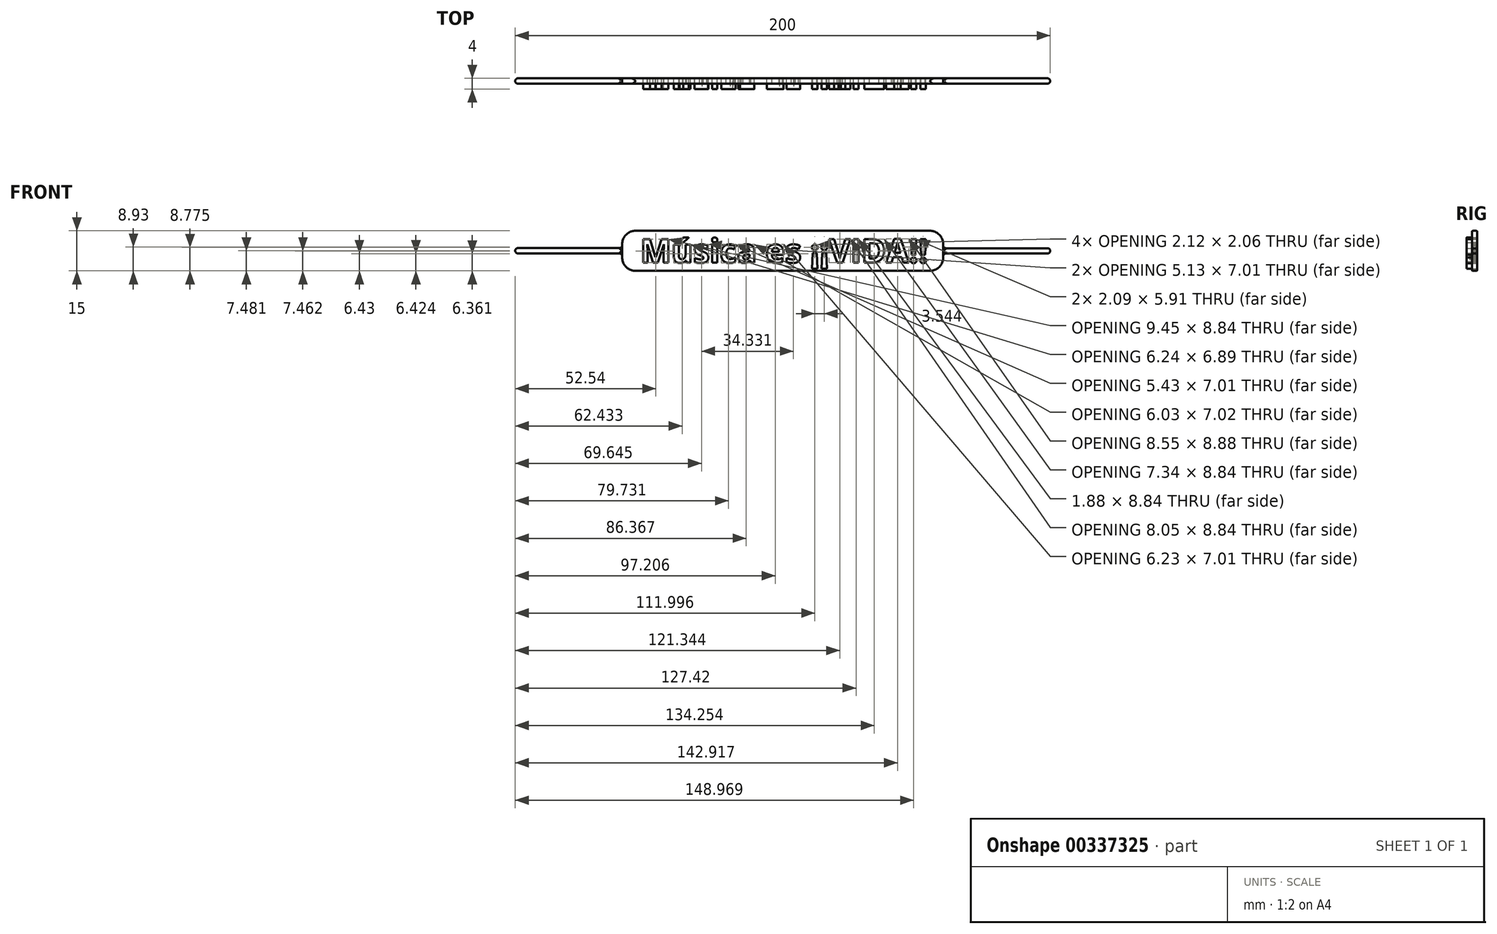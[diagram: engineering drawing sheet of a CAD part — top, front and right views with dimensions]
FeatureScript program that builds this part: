
annotation { "Feature Type Name" : "Feature", "Feature Type Description" : "" }
export const myFeature = defineFeature(function(context is Context, id is Id, definition is map)
    precondition{}
    {
        {
            var Q0;
            Q0=qCreatedBy(makeId("Front.planeOp"),FACE);
            var sketch = newSketch(context, id + "F0", { "sketchPlane" : qUnion([Q0])});
            skLineSegment(sketch, "E0.bottom", {"start": v(-55, 7.5) * mm, "end": v(55, 7.5) * mm});
            skLineSegment(sketch, "E0.top", {"start": v(-55, -7.5) * mm, "end": v(55, -7.5) * mm});
            skLineSegment(sketch, "E0.left", {"start": v(-60, 2.5) * mm, "end": v(-60, -2.5) * mm});
            skLineSegment(sketch, "E0.right", {"start": v(60, 2.5) * mm, "end": v(60, -2.5) * mm});
            skPoint(sketch, "E1.visualSharp", {"position": v(-60, 7.5) * mm});
            skArc(sketch, "E1.filletArc", {"start": v(-55, 7.5) * mm, "mid": v(-58.54, 6.04) * mm, "end": v(-60, 2.5) * mm});
            skPoint(sketch, "E2.visualSharp", {"position": v(-60, -7.5) * mm});
            skArc(sketch, "E2.filletArc", {"start": v(-60, -2.5) * mm, "mid": v(-58.54, -6.04) * mm, "end": v(-55, -7.5) * mm});
            skPoint(sketch, "E3.visualSharp", {"position": v(60, -7.5) * mm});
            skArc(sketch, "E3.filletArc", {"start": v(55, -7.5) * mm, "mid": v(58.54, -6.04) * mm, "end": v(60, -2.5) * mm});
            skPoint(sketch, "E4.visualSharp", {"position": v(60, 7.5) * mm});
            skArc(sketch, "E4.filletArc", {"start": v(60, 2.5) * mm, "mid": v(58.54, 6.04) * mm, "end": v(55, 7.5) * mm});
            skText(sketch, "E5", { "text": "Música es ¡¡VIDA!!", "fontName": "OpenSans-Bold.ttf"});
            const initialGuessF0  = {"E5": [-0.0533, -0.00446, 1, 0, 0.00892]};
            skSetInitialGuess(sketch, initialGuessF0);
            skSolve(sketch);
        }
        {
            var Q0;
            Q0 = qSketchRegion(id + "F0", true);
            var Q1;
            Q1=makeQuery(id+"F0.imprint","IMPRINT",FACE,{"disambiguationData":[TD([[makeQuery(id+"F0.imprint","IMPRINT",EDGE,{"derivedFrom":sQuery(id+"F0.wireOp",EDGE,"E5.sketch_text.stroke-110")}),1.0]])]});
            var Q2;
            Q2=makeQuery(id+"F0.imprint","IMPRINT",FACE,{"disambiguationData":[TD([[makeQuery(id+"F0.imprint","IMPRINT",EDGE,{"derivedFrom":sQuery(id+"F0.wireOp",EDGE,"E5.sketch_text.stroke-117")}),1.0]])]});
            var Q3;
            Q3=makeQuery(id+"F0.imprint","IMPRINT",FACE,{"disambiguationData":[TD([[makeQuery(id+"F0.imprint","IMPRINT",EDGE,{"derivedFrom":sQuery(id+"F0.wireOp",EDGE,"E5.sketch_text.stroke-208")}),1.0]])]});
            var Q4;
            Q4=makeQuery(id+"F0.imprint","IMPRINT",FACE,{"disambiguationData":[TD([[makeQuery(id+"F0.imprint","IMPRINT",EDGE,{"derivedFrom":sQuery(id+"F0.wireOp",EDGE,"E5.sketch_text.stroke-221")}),1.0]])]});
            extrude(context, id + "F1", {"entities" : qUnion([Q0, Q1, Q2, Q3, Q4]), "depth" : 2 * mm});
        }
        {
            var Q0;
            Q0=makeQuery(id+"F0.imprint","IMPRINT",FACE,{"disambiguationData":[TD([[makeQuery(id+"F0.imprint","IMPRINT",EDGE,{"derivedFrom":sQuery(id+"F0.wireOp",EDGE,"E5.sketch_text.stroke-0")}),-1.0]])]});
            var Q1;
            Q1=makeQuery(id+"F0.imprint","IMPRINT",FACE,{"disambiguationData":[TD([[makeQuery(id+"F0.imprint","IMPRINT",EDGE,{"derivedFrom":sQuery(id+"F0.wireOp",EDGE,"E5.sketch_text.stroke-19")}),-1.0]])]});
            var Q2;
            Q2=makeQuery(id+"F0.imprint","IMPRINT",FACE,{"disambiguationData":[TD([[makeQuery(id+"F0.imprint","IMPRINT",EDGE,{"derivedFrom":sQuery(id+"F0.wireOp",EDGE,"E5.sketch_text.stroke-36")}),-1.0]])]});
            var Q3;
            Q3=makeQuery(id+"F0.imprint","IMPRINT",FACE,{"disambiguationData":[TD([[makeQuery(id+"F0.imprint","IMPRINT",EDGE,{"derivedFrom":sQuery(id+"F0.wireOp",EDGE,"E5.sketch_text.stroke-43")}),-1.0]])]});
            var Q4;
            Q4=makeQuery(id+"F0.imprint","IMPRINT",FACE,{"disambiguationData":[TD([[makeQuery(id+"F0.imprint","IMPRINT",EDGE,{"derivedFrom":sQuery(id+"F0.wireOp",EDGE,"E5.sketch_text.stroke-69")}),-1.0]])]});
            var Q5;
            Q5=makeQuery(id+"F0.imprint","IMPRINT",FACE,{"disambiguationData":[TD([[makeQuery(id+"F0.imprint","IMPRINT",EDGE,{"derivedFrom":sQuery(id+"F0.wireOp",EDGE,"E5.sketch_text.stroke-74")}),-1.0]])]});
            var Q6;
            Q6=makeQuery(id+"F0.imprint","IMPRINT",FACE,{"disambiguationData":[TD([[makeQuery(id+"F0.imprint","IMPRINT",EDGE,{"derivedFrom":sQuery(id+"F0.wireOp",EDGE,"E5.sketch_text.stroke-78")}),-1.0]])]});
            var Q7;
            Q7=makeQuery(id+"F0.imprint","IMPRINT",FACE,{"disambiguationData":[TD([[makeQuery(id+"F0.imprint","IMPRINT",EDGE,{"derivedFrom":sQuery(id+"F0.wireOp",EDGE,"E5.sketch_text.stroke-92")}),-1.0]])]});
            var Q8;
            Q8=makeQuery(id+"F0.imprint","IMPRINT",FACE,{"disambiguationData":[TD([[makeQuery(id+"F0.imprint","IMPRINT",EDGE,{"derivedFrom":sQuery(id+"F0.wireOp",EDGE,"E5.sketch_text.stroke-117")}),-1.0]])]});
            var Q9;
            Q9=makeQuery(id+"F0.imprint","IMPRINT",FACE,{"disambiguationData":[TD([[makeQuery(id+"F0.imprint","IMPRINT",EDGE,{"derivedFrom":sQuery(id+"F0.wireOp",EDGE,"E5.sketch_text.stroke-137")}),-1.0]])]});
            var Q10;
            Q10=makeQuery(id+"F0.imprint","IMPRINT",FACE,{"disambiguationData":[TD([[makeQuery(id+"F0.imprint","IMPRINT",EDGE,{"derivedFrom":sQuery(id+"F0.wireOp",EDGE,"E5.sketch_text.stroke-167")}),-1.0]])]});
            var Q11;
            Q11=makeQuery(id+"F0.imprint","IMPRINT",FACE,{"disambiguationData":[TD([[makeQuery(id+"F0.imprint","IMPRINT",EDGE,{"derivedFrom":sQuery(id+"F0.wireOp",EDGE,"E5.sketch_text.stroke-179")}),-1.0]])]});
            var Q12;
            Q12=makeQuery(id+"F0.imprint","IMPRINT",FACE,{"disambiguationData":[TD([[makeQuery(id+"F0.imprint","IMPRINT",EDGE,{"derivedFrom":sQuery(id+"F0.wireOp",EDGE,"E5.sketch_text.stroke-175")}),-1.0]])]});
            var Q13;
            Q13=makeQuery(id+"F0.imprint","IMPRINT",FACE,{"disambiguationData":[TD([[makeQuery(id+"F0.imprint","IMPRINT",EDGE,{"derivedFrom":sQuery(id+"F0.wireOp",EDGE,"E5.sketch_text.stroke-163")}),-1.0]])]});
            var Q14;
            Q14=makeQuery(id+"F0.imprint","IMPRINT",FACE,{"disambiguationData":[TD([[makeQuery(id+"F0.imprint","IMPRINT",EDGE,{"derivedFrom":sQuery(id+"F0.wireOp",EDGE,"E5.sketch_text.stroke-187")}),-1.0]])]});
            var Q15;
            Q15=makeQuery(id+"F0.imprint","IMPRINT",FACE,{"disambiguationData":[TD([[makeQuery(id+"F0.imprint","IMPRINT",EDGE,{"derivedFrom":sQuery(id+"F0.wireOp",EDGE,"E5.sketch_text.stroke-197")}),-1.0]])]});
            var Q16;
            Q16=makeQuery(id+"F0.imprint","IMPRINT",FACE,{"disambiguationData":[TD([[makeQuery(id+"F0.imprint","IMPRINT",EDGE,{"derivedFrom":sQuery(id+"F0.wireOp",EDGE,"E5.sketch_text.stroke-201")}),-1.0]])]});
            var Q17;
            Q17=makeQuery(id+"F0.imprint","IMPRINT",FACE,{"disambiguationData":[TD([[makeQuery(id+"F0.imprint","IMPRINT",EDGE,{"derivedFrom":sQuery(id+"F0.wireOp",EDGE,"E5.sketch_text.stroke-213")}),-1.0]])]});
            var Q18;
            Q18=makeQuery(id+"F0.imprint","IMPRINT",FACE,{"disambiguationData":[TD([[makeQuery(id+"F0.imprint","IMPRINT",EDGE,{"derivedFrom":sQuery(id+"F0.wireOp",EDGE,"E5.sketch_text.stroke-225")}),-1.0]])]});
            var Q19;
            Q19=makeQuery(id+"F0.imprint","IMPRINT",FACE,{"disambiguationData":[TD([[makeQuery(id+"F0.imprint","IMPRINT",EDGE,{"derivedFrom":sQuery(id+"F0.wireOp",EDGE,"E5.sketch_text.stroke-237")}),-1.0]])]});
            var Q20;
            Q20=makeQuery(id+"F0.imprint","IMPRINT",FACE,{"disambiguationData":[TD([[makeQuery(id+"F0.imprint","IMPRINT",EDGE,{"derivedFrom":sQuery(id+"F0.wireOp",EDGE,"E5.sketch_text.stroke-241")}),-1.0]])]});
            var Q21;
            Q21=makeQuery(id+"F0.imprint","IMPRINT",FACE,{"disambiguationData":[TD([[makeQuery(id+"F0.imprint","IMPRINT",EDGE,{"derivedFrom":sQuery(id+"F0.wireOp",EDGE,"E5.sketch_text.stroke-229")}),-1.0]])]});
            extrude(context, id + "F2", {"entities" : qUnion([Q0, Q1, Q2, Q3, Q4, Q5, Q6, Q7, Q8, Q9, Q10, Q11, Q12, Q13, Q14, Q15, Q16, Q17, Q18, Q19, Q20, Q21]), "depth" : 4 * mm});
        }
        {
            var Q0;
            Q0=makeQuery(id+"F1.opExtrude","SWEPT_FACE",FACE,{"disambiguationData":[OSD([sQuery(id+"F0.wireOp",EDGE,"E0.left")])]});
            var sketch = newSketch(context, id + "F3", { "sketchPlane" : qUnion([Q0])});
            skCircle(sketch, "E6", {"center": v(1, 0.02) * mm, "radius": 1 * mm});
            skPoint(sketch, "E6.first.point", {"position": v(0, 0) * mm});
            skPoint(sketch, "E6.second.point", {"position": v(2, 0) * mm});
            skPoint(sketch, "E6.third.point", {"position": v(1.3, 0.97) * mm});
            skSolve(sketch);
        }
        {
            var Q0;
            {var subQ0=sQuery(id+"F3.wireOp",EDGE,"E6");var subQ1=sQuery(id+"F0.wireOp",EDGE,"E0.left");var subQ2=makeQuery(id+"F1.opExtrude","CAP_EDGE",EDGE,{"disambiguationData":[OSD([subQ1])],"isStart":true});var subQ3=makeQuery(id+"F3.imprint","INTERSECT",VERTEX,{"disambiguationData":[OD(0.0)],"derivedFrom":[subQ2,subQ0]});Q0=makeQuery(id+"F3.imprint","IMPRINT",FACE,{"disambiguationData":[TD([[makeQuery(id+"F3.imprint","IMPRINT",EDGE,{"disambiguationData":[TD([[subQ3,1.0]])],"derivedFrom":subQ0}),1.0]])]});}
            extrude(context, id + "F4", {"entities" : qUnion([Q0]), "operationType" : NewBodyOperationType.ADD, "depth" : 40 * mm});
        }
        {
            var Q0;
            Q0=makeQuery(id+"F1.opExtrude","SWEPT_FACE",FACE,{"disambiguationData":[OSD([sQuery(id+"F0.wireOp",EDGE,"E0.right")])]});
            var sketch = newSketch(context, id + "F5", { "sketchPlane" : qUnion([Q0])});
            skCircle(sketch, "E7", {"center": v(-1, -0.02) * mm, "radius": 1 * mm});
            skPoint(sketch, "E7.first.point", {"position": v(-2, 0) * mm});
            skPoint(sketch, "E7.second.point", {"position": v(0, 0) * mm});
            skPoint(sketch, "E7.third.point", {"position": v(-0.56, 0.88) * mm});
            skSolve(sketch);
        }
        {
            var Q0;
            {var subQ0=sQuery(id+"F5.wireOp",EDGE,"E7");var subQ1=sQuery(id+"F0.wireOp",EDGE,"E0.right");var subQ2=makeQuery(id+"F1.opExtrude","CAP_EDGE",EDGE,{"disambiguationData":[OSD([subQ1])],"isStart":false});var subQ3=makeQuery(id+"F5.imprint","INTERSECT",VERTEX,{"disambiguationData":[OD(0.0)],"derivedFrom":[subQ2,subQ0]});Q0=makeQuery(id+"F5.imprint","IMPRINT",FACE,{"disambiguationData":[TD([[makeQuery(id+"F5.imprint","IMPRINT",EDGE,{"disambiguationData":[TD([[subQ3,1.0]])],"derivedFrom":subQ0}),1.0]])]});}
            extrude(context, id + "F6", {"entities" : qUnion([Q0]), "operationType" : NewBodyOperationType.ADD, "depth" : 40 * mm});
        }
        {
            var Q0;
            {var subQ0=sQuery(id+"F5.wireOp",EDGE,"E7");var subQ1=sQuery(id+"F0.wireOp",EDGE,"E0.right");Q0=makeQuery(id+"F6.opExtrude","CAP_EDGE",EDGE,{"disambiguationData":[OSD([subQ0]),TDD([makeQuery(id+"F5.imprint","IMPRINT",EDGE,{"disambiguationData":[TD([[makeQuery(id+"F5.imprint","INTERSECT",VERTEX,{"disambiguationData":[OD(1.0)],"derivedFrom":[makeQuery(id+"F1.opExtrude","CAP_EDGE",EDGE,{"disambiguationData":[OSD([subQ1])],"isStart":false}),subQ0]}),-1.0]])],"derivedFrom":subQ0})])],"isStart":true});}
            var Q1;
            {var subQ0=sQuery(id+"F5.wireOp",EDGE,"E7");var subQ1=sQuery(id+"F0.wireOp",EDGE,"E0.right");Q1=makeQuery(id+"F6.opExtrude","CAP_EDGE",EDGE,{"disambiguationData":[OSD([subQ0]),TDD([makeQuery(id+"F5.imprint","IMPRINT",EDGE,{"disambiguationData":[TD([[makeQuery(id+"F5.imprint","INTERSECT",VERTEX,{"disambiguationData":[OD(0.0)],"derivedFrom":[makeQuery(id+"F1.opExtrude","CAP_EDGE",EDGE,{"disambiguationData":[OSD([subQ1])],"isStart":false}),subQ0]}),1.0]])],"derivedFrom":subQ0})])],"isStart":true});}
            var Q2;
            Q2=makeQuery(id+"F6.opExtrude","CAP_FACE",FACE,{"disambiguationData":[OSD([sQuery(id+"F0.wireOp",EDGE,"E0.right"),sQuery(id+"F5.wireOp",EDGE,"E7")])],"isStart":false});
            var Q3;
            {var subQ0=sQuery(id+"F3.wireOp",EDGE,"E6");var subQ1=sQuery(id+"F0.wireOp",EDGE,"E0.left");Q3=makeQuery(id+"F4.opExtrude","CAP_EDGE",EDGE,{"disambiguationData":[OSD([subQ0]),TDD([makeQuery(id+"F3.imprint","IMPRINT",EDGE,{"disambiguationData":[TD([[makeQuery(id+"F3.imprint","INTERSECT",VERTEX,{"disambiguationData":[OD(1.0)],"derivedFrom":[makeQuery(id+"F1.opExtrude","CAP_EDGE",EDGE,{"disambiguationData":[OSD([subQ1])],"isStart":true}),subQ0]}),-1.0]])],"derivedFrom":subQ0})])],"isStart":true});}
            var Q4;
            {var subQ0=sQuery(id+"F3.wireOp",EDGE,"E6");var subQ1=sQuery(id+"F0.wireOp",EDGE,"E0.left");Q4=makeQuery(id+"F4.opExtrude","CAP_EDGE",EDGE,{"disambiguationData":[OSD([subQ0]),TDD([makeQuery(id+"F3.imprint","IMPRINT",EDGE,{"disambiguationData":[TD([[makeQuery(id+"F3.imprint","INTERSECT",VERTEX,{"disambiguationData":[OD(0.0)],"derivedFrom":[makeQuery(id+"F1.opExtrude","CAP_EDGE",EDGE,{"disambiguationData":[OSD([subQ1])],"isStart":true}),subQ0]}),1.0]])],"derivedFrom":subQ0})])],"isStart":true});}
            var Q5;
            Q5=makeQuery(id+"F4.opExtrude","CAP_FACE",FACE,{"disambiguationData":[OSD([sQuery(id+"F0.wireOp",EDGE,"E0.left"),sQuery(id+"F3.wireOp",EDGE,"E6")])],"isStart":false});
            var Q6;
            Q6=makeQuery(id+"F1.opExtrude","SWEPT_FACE",FACE,{"disambiguationData":[OSD([sQuery(id+"F0.wireOp",EDGE,"E0.top")])]});
            var Q7;
            Q7=makeQuery(id+"F1.opExtrude","SWEPT_FACE",FACE,{"disambiguationData":[OSD([sQuery(id+"F0.wireOp",EDGE,"E0.bottom")])]});
            fillet(context, id + "F7", {"entities" : qUnion([Q0, Q1, Q2, Q3, Q4, Q5, Q6, Q7]), "radius" : 1 * mm, "tangentPropagation" : true, "allowEdgeOverflow" : false});
        }
    });
